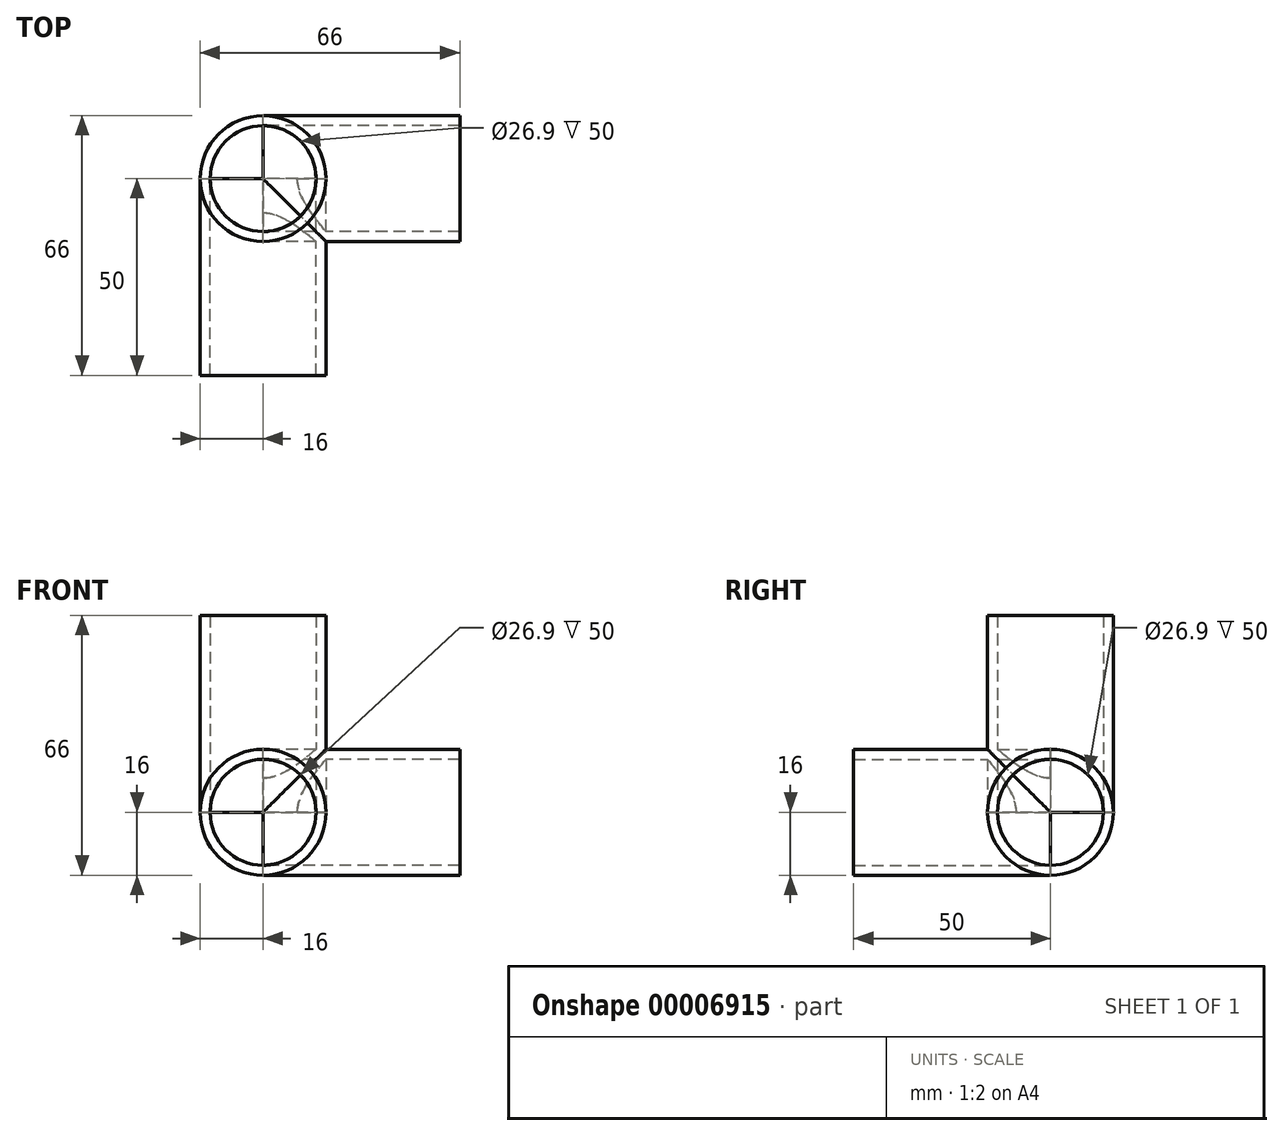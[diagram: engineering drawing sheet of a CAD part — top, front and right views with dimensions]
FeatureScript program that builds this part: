
annotation { "Feature Type Name" : "Feature", "Feature Type Description" : "" }
export const myFeature = defineFeature(function(context is Context, id is Id, definition is map)
    precondition{}
    {
        {
            var Q0;
            Q0=qCreatedBy(makeId("Top.planeOp"),FACE);
            var sketch = newSketch(context, id + "F0", { "sketchPlane" : qUnion([Q0])});
            skCircle(sketch, "E0", {"center": v(0, 0) * mm, "radius": 13.45 * mm});
            skCircle(sketch, "E1", {"center": v(0, 0) * mm, "radius": 16 * mm});
            skSolve(sketch);
        }
        {
            var Q0;
            Q0=makeQuery(id+"F0.imprint","IMPRINT",FACE,{"disambiguationData":[TD([[makeQuery(id+"F0.imprint","IMPRINT",EDGE,{"derivedFrom":sQuery(id+"F0.wireOp",EDGE,"E0")}),-1.0]])]});
            extrude(context, id + "F1", {"entities" : qUnion([Q0]), "depth" : 50 * mm});
        }
        {
            var Q0;
            Q0=qCreatedBy(makeId("Front.planeOp"),FACE);
            var sketch = newSketch(context, id + "F2", { "sketchPlane" : qUnion([Q0])});
            skCircle(sketch, "E2", {"center": v(0, 0) * mm, "radius": 16 * mm});
            skCircle(sketch, "E3", {"center": v(0, 0) * mm, "radius": 13.45 * mm});
            skSolve(sketch);
        }
        {
            var Q0;
            Q0=makeQuery(id+"F2.imprint","IMPRINT",FACE,{"disambiguationData":[TD([[makeQuery(id+"F2.imprint","IMPRINT",EDGE,{"derivedFrom":sQuery(id+"F2.wireOp",EDGE,"E2")}),1.0]])]});
            extrude(context, id + "F3", {"entities" : qUnion([Q0]), "operationType" : NewBodyOperationType.ADD, "depth" : 50 * mm});
        }
        {
            var Q0;
            Q0=qCreatedBy(makeId("Right.planeOp"),FACE);
            var sketch = newSketch(context, id + "F4", { "sketchPlane" : qUnion([Q0])});
            skCircle(sketch, "E4", {"center": v(0, 0) * mm, "radius": 13.45 * mm});
            skCircle(sketch, "E5", {"center": v(0, 0) * mm, "radius": 16 * mm});
            skSolve(sketch);
        }
        {
            var Q0;
            Q0 = qSketchRegion(id + "F4", true);
            extrude(context, id + "F5", {"entities" : qUnion([Q0]), "operationType" : NewBodyOperationType.ADD, "depth" : 50 * mm});
        }
    });
